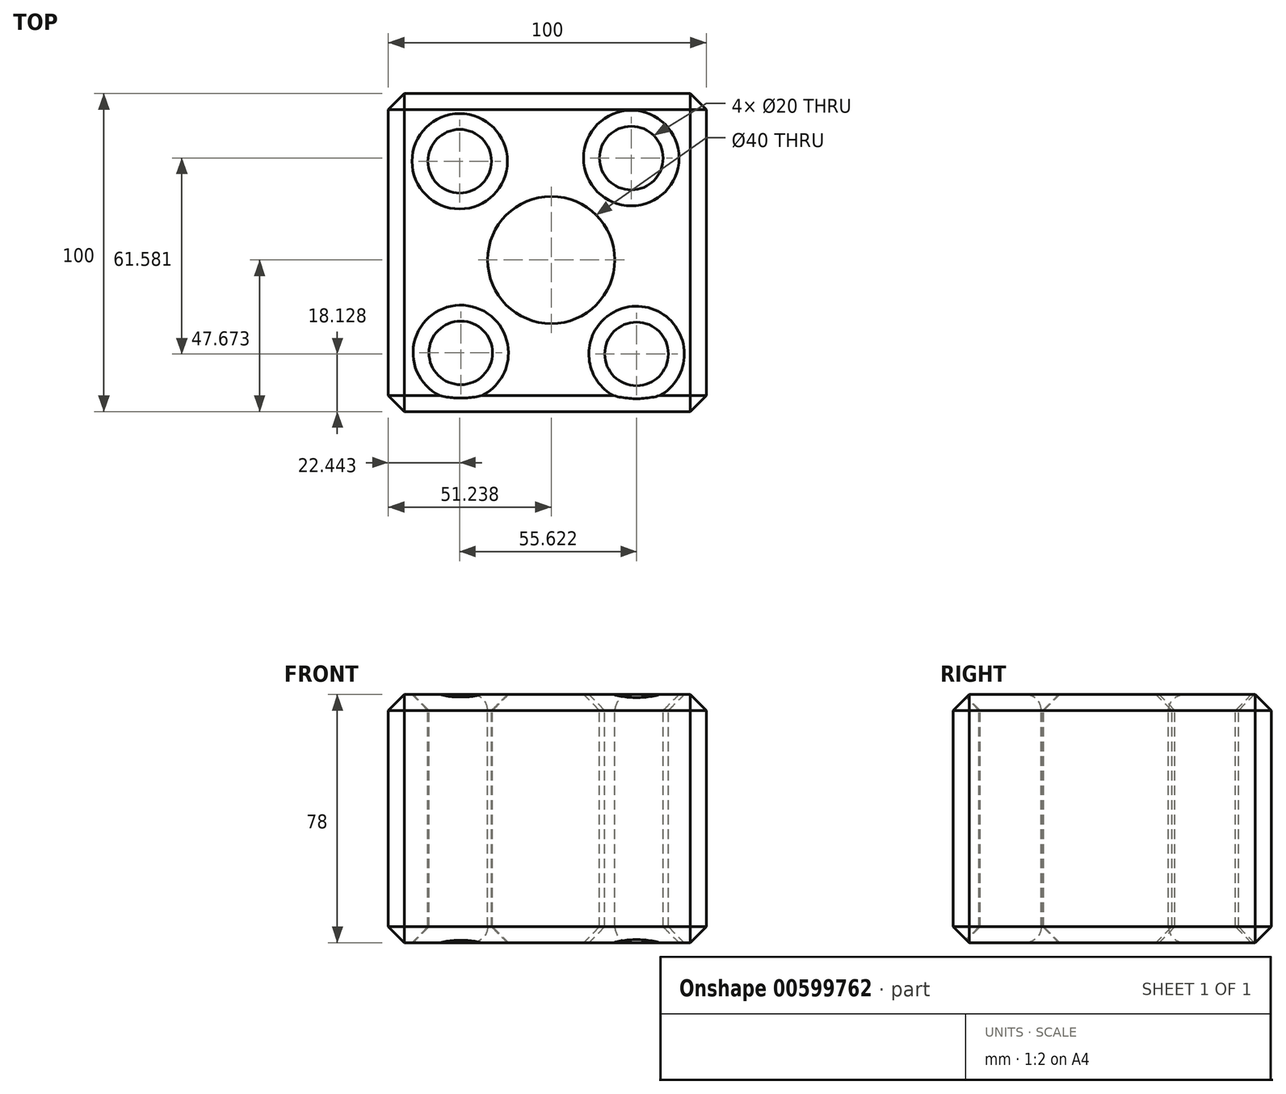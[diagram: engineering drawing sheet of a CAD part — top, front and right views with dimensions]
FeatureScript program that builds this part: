
annotation { "Feature Type Name" : "Feature", "Feature Type Description" : "" }
export const myFeature = defineFeature(function(context is Context, id is Id, definition is map)
    precondition{}
    {
        {
            var Q0;
            Q0=qCreatedBy(makeId("Top.planeOp"),FACE);
            var sketch = newSketch(context, id + "F0", { "sketchPlane" : qUnion([Q0])});
            skLineSegment(sketch, "E0.bottom", {"start": v(0, 0) * mm, "end": v(-100, 0) * mm});
            skLineSegment(sketch, "E0.top", {"start": v(0, 100) * mm, "end": v(-100, 100) * mm});
            skLineSegment(sketch, "E0.left", {"start": v(0, 0) * mm, "end": v(0, 100) * mm});
            skLineSegment(sketch, "E0.right", {"start": v(-100, 0) * mm, "end": v(-100, 100) * mm});
            skCircle(sketch, "E1", {"center": v(-77.56, 78.72) * mm, "radius": 10 * mm});
            skCircle(sketch, "E2", {"center": v(-23.6, 79.7) * mm, "radius": 10 * mm});
            skCircle(sketch, "E3", {"center": v(-77.23, 18.46) * mm, "radius": 10 * mm});
            skCircle(sketch, "E4", {"center": v(-21.94, 18.13) * mm, "radius": 10 * mm});
            skCircle(sketch, "E5", {"center": v(-48.76, 47.67) * mm, "radius": 20 * mm});
            skSolve(sketch);
        }
        {
            var Q0;
            Q0 = qSketchRegion(id + "F0", true);
            extrude(context, id + "F1", {"entities" : qUnion([Q0]), "oppositeDirection" : true, "depth" : 78 * mm, "offsetDistance" : 25 * mm});
        }
        {
            var Q0;
            Q0=makeQuery(id+"F1.opExtrude","CAP_EDGE",EDGE,{"disambiguationData":[OSD([sQuery(id+"F0.wireOp",EDGE,"E1")])],"isStart":true});
            var Q1;
            Q1=makeQuery(id+"F1.opExtrude","CAP_EDGE",EDGE,{"disambiguationData":[OSD([sQuery(id+"F0.wireOp",EDGE,"E2")])],"isStart":true});
            var Q2;
            Q2=makeQuery(id+"F1.opExtrude","CAP_EDGE",EDGE,{"disambiguationData":[OSD([sQuery(id+"F0.wireOp",EDGE,"E4")])],"isStart":true});
            var Q3;
            Q3=makeQuery(id+"F1.opExtrude","CAP_EDGE",EDGE,{"disambiguationData":[OSD([sQuery(id+"F0.wireOp",EDGE,"E3")])],"isStart":true});
            var Q4;
            Q4=makeQuery(id+"F1.opExtrude","CAP_EDGE",EDGE,{"disambiguationData":[OSD([sQuery(id+"F0.wireOp",EDGE,"E3")])],"isStart":false});
            var Q5;
            Q5=makeQuery(id+"F1.opExtrude","CAP_EDGE",EDGE,{"disambiguationData":[OSD([sQuery(id+"F0.wireOp",EDGE,"E4")])],"isStart":false});
            var Q6;
            Q6=makeQuery(id+"F1.opExtrude","CAP_EDGE",EDGE,{"disambiguationData":[OSD([sQuery(id+"F0.wireOp",EDGE,"E2")])],"isStart":false});
            var Q7;
            Q7=makeQuery(id+"F1.opExtrude","CAP_EDGE",EDGE,{"disambiguationData":[OSD([sQuery(id+"F0.wireOp",EDGE,"E1")])],"isStart":false});
            var Q8;
            Q8=makeQuery(id+"F1.opExtrude","SWEPT_EDGE",EDGE,{"disambiguationData":[OSD([sQuery(id+"F0.wireOp",EDGE,"E0.top"),sQuery(id+"F0.wireOp",EDGE,"E0.right")])]});
            var Q9;
            Q9=makeQuery(id+"F1.opExtrude","SWEPT_EDGE",EDGE,{"disambiguationData":[OSD([sQuery(id+"F0.wireOp",EDGE,"E0.top"),sQuery(id+"F0.wireOp",EDGE,"E0.left")])]});
            var Q10;
            Q10=makeQuery(id+"F1.opExtrude","SWEPT_EDGE",EDGE,{"disambiguationData":[OSD([sQuery(id+"F0.wireOp",EDGE,"E0.bottom"),sQuery(id+"F0.wireOp",EDGE,"E0.left")])]});
            var Q11;
            Q11=makeQuery(id+"F1.opExtrude","SWEPT_EDGE",EDGE,{"disambiguationData":[OSD([sQuery(id+"F0.wireOp",EDGE,"E0.bottom"),sQuery(id+"F0.wireOp",EDGE,"E0.right")])]});
            var Q12;
            Q12=makeQuery(id+"F1.opExtrude","CAP_EDGE",EDGE,{"disambiguationData":[OSD([sQuery(id+"F0.wireOp",EDGE,"E0.bottom")])],"isStart":false});
            var Q13;
            Q13=makeQuery(id+"F1.opExtrude","CAP_EDGE",EDGE,{"disambiguationData":[OSD([sQuery(id+"F0.wireOp",EDGE,"E0.right")])],"isStart":false});
            var Q14;
            Q14=makeQuery(id+"F1.opExtrude","CAP_EDGE",EDGE,{"disambiguationData":[OSD([sQuery(id+"F0.wireOp",EDGE,"E0.top")])],"isStart":false});
            var Q15;
            Q15=makeQuery(id+"F1.opExtrude","CAP_EDGE",EDGE,{"disambiguationData":[OSD([sQuery(id+"F0.wireOp",EDGE,"E0.left")])],"isStart":false});
            var Q16;
            Q16=makeQuery(id+"F1.opExtrude","CAP_EDGE",EDGE,{"disambiguationData":[OSD([sQuery(id+"F0.wireOp",EDGE,"E0.left")])],"isStart":true});
            var Q17;
            Q17=makeQuery(id+"F1.opExtrude","CAP_EDGE",EDGE,{"disambiguationData":[OSD([sQuery(id+"F0.wireOp",EDGE,"E0.bottom")])],"isStart":true});
            var Q18;
            Q18=makeQuery(id+"F1.opExtrude","CAP_EDGE",EDGE,{"disambiguationData":[OSD([sQuery(id+"F0.wireOp",EDGE,"E0.right")])],"isStart":true});
            var Q19;
            Q19=makeQuery(id+"F1.opExtrude","CAP_EDGE",EDGE,{"disambiguationData":[OSD([sQuery(id+"F0.wireOp",EDGE,"E0.top")])],"isStart":true});
            chamfer(context, id + "F2", {"entities" : qUnion([Q0, Q1, Q2, Q3, Q4, Q5, Q6, Q7, Q8, Q9, Q10, Q11, Q12, Q13, Q14, Q15, Q16, Q17, Q18, Q19]), "width" : 5 * mm, "tangentPropagation" : true});
        }
        {
            var Q0;
            Q0=makeQuery(id+"F1.opExtrude","CAP_EDGE",EDGE,{"disambiguationData":[OSD([sQuery(id+"F0.wireOp",EDGE,"E5")])],"isStart":false});
            var Q1;
            Q1=makeQuery(id+"F1.opExtrude","CAP_EDGE",EDGE,{"disambiguationData":[OSD([sQuery(id+"F0.wireOp",EDGE,"E5")])],"isStart":true});
            fillet(context, id + "F3", {"entities" : qUnion([Q0, Q1]), "radius" : 5 * mm, "tangentPropagation" : true, "allowEdgeOverflow" : false});
        }
    });
